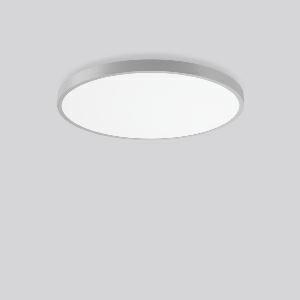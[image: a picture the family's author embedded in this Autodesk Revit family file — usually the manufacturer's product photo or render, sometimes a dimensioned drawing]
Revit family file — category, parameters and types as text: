
# Revit family: triona_round_a_312388_004_1_730_41b7
name_source: partatom
category: Lighting Fixtures
units: mm (PartAtom-declared; Revit-internal decimal feet)

## family parameters
Cut with Voids When Loaded = No
Host = Face
Light Source = No
Part Type = Normal
Room Calculation Point = No
Round Connector Dimension = Use Diameter
Shared = No

## types (1)
- TRIONA round A (1 x LED Modul 840, 12900 lm, 4000)
    Apparent Load = 133 VA
    CIE Flux Codes = 49 80 96 71 100
    Color Rendering = 80
    Color Temperature = 4000
    Default Elevation = 1800 mm
    Description = Series: TRIONA round
Decorative round LED surface-mounted luminaire. Flat, seamless frame: aluminium extrusion profile, powder coated. Cover made of sheet steel, powder-coated. Direct light emission through a diffuser plastic opal. Indirect light emission through a flush diffuser made of satin-finish plastic. Lightguide and diffuser made of non-yellowing plastic (PMMA). Lateral light emission (RZB SIDELITE technology) for above-average homogeneous light distribution. Direct 70%, indirect 30% light emission. Suitable for Ceiling mounting, Wall (surface). Tool-free mounting via bayonet connection. Electronic ballast included. Very easy installation thanks to Plug+Play connection. With Casambi smart+free Bluetooth control for wireless network and operation using Android / iOS devices, free app available for download. 
Colour: silver, matt (approx. RAL 9006)
Diameter: 845 mm
Height: 88 mm
Lamp: LED
Socket: without socket
Colour temperature: 4000K
Colour rendering index (CRI): 80
System power: 133 W
Rated luminous flux: 12900 lm
Luminous efficiency: 97 lm/W
Control gear: Dimmable Bluetooth converter
Protection class: I
Type of protection: IP 20
    Height = 88 mm
    Lamp = 1 x LED Modul 840
    Lamp Light Flux = 12900 lm
    Lamp count = 1
    Length = 845 mm
    Lifetime = 50000 h
    Luminous efficacy = 97 lm/W
    Manufacturer = RZB
    ModVariant = No
    Model = 312388.004.1.730
    Mounting Place = Ceiling
    Mounting Type = Surface mounted
    Number of Poles = 1
    OnlyDefault = Yes
    Power Factor = 1
    Product Name = TRIONA round A
    Product group = Surface mounted modular luminaires
    ProductGroupID = 306
    Protection Class = Protection class I
    Protection Degree = IP 20
    RLX_Detail_Level = 1
    RLX_Emergency_Light_Flux = 0 lm
    RLX_Emergency_Type = 0
    RLX_Emergency_Type_DB = No
    RlxData = <blob elided: 42425 chars, md5=07867042>
    Socket = socket
    Standby Power = 0 W
    System Light Flux = 12900 lm
    System Power = 133 W
    Type Comments = Product without accessories
    Type Image = 312388.004.jpg
    URL = http://relux.com
    VarID = ---
    Voltage = 230 V
    Voltage Range = 220-240 V
    Weight = 0.00 kg
    Width = 0 mm  [stored 0 ft]

note: [stored X ft] marks values corroborated as IEEE doubles in the binary element streams (Revit-internal decimal feet)

## geometry (parser evidence)
native form markers: Blend x4, Sweep x11
no freeform markers — native parametric forms only
